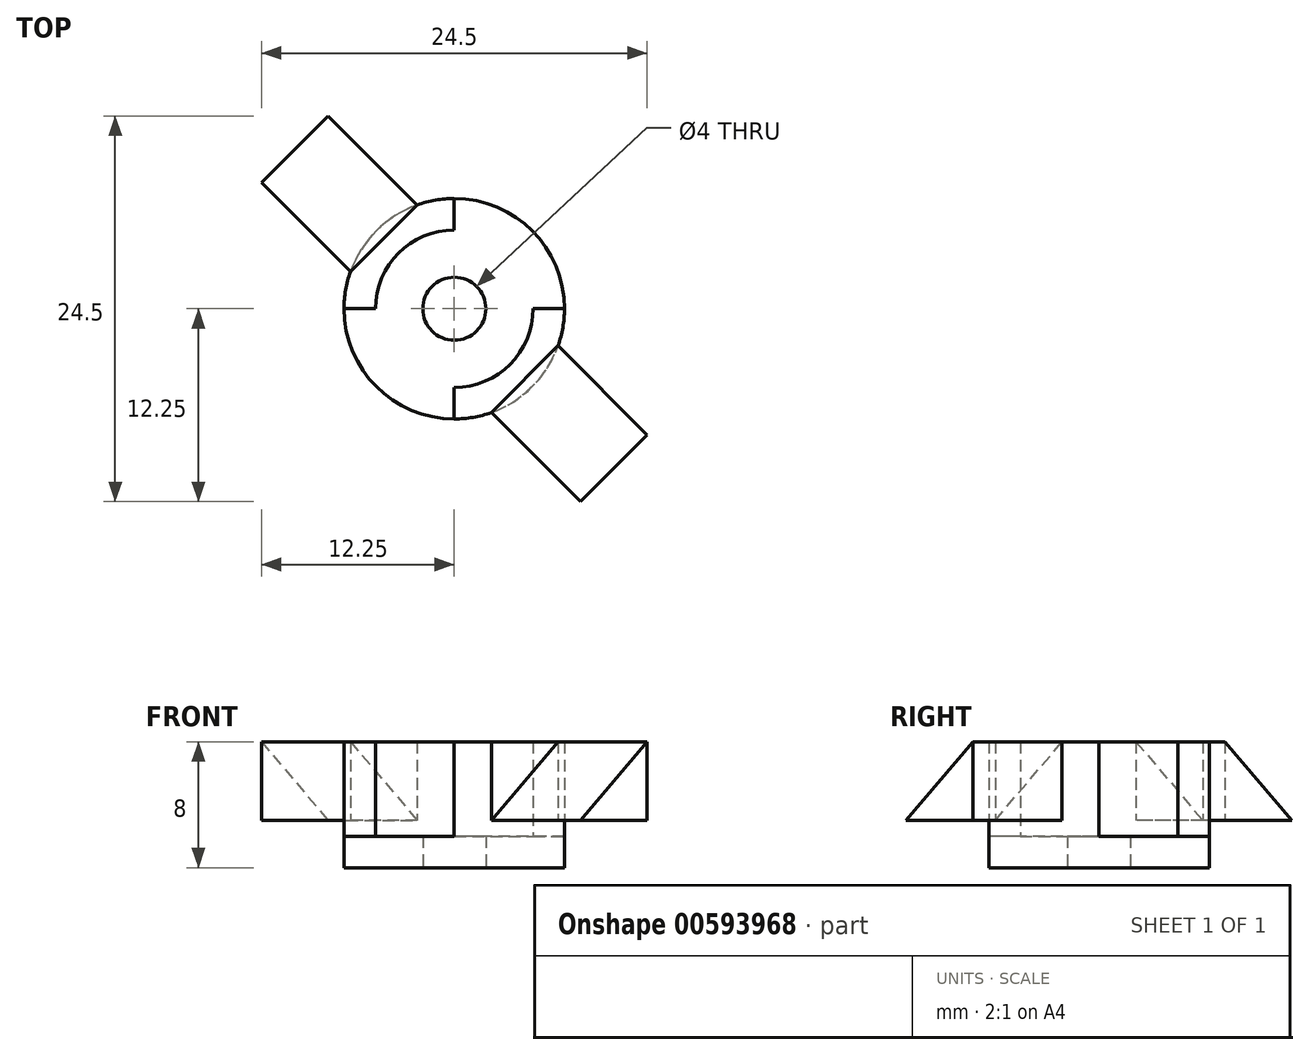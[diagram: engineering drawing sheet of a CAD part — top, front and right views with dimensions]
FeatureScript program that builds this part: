
annotation { "Feature Type Name" : "Feature", "Feature Type Description" : "" }
export const myFeature = defineFeature(function(context is Context, id is Id, definition is map)
    precondition{}
    {
        {
            var Q0;
            Q0=qCreatedBy(makeId("Top.planeOp"),FACE);
            var sketch = newSketch(context, id + "F0", { "sketchPlane" : qUnion([Q0])});
            skCircle(sketch, "E0", {"center": v(0, 0) * mm, "radius": 5 * mm});
            skCircle(sketch, "E1", {"center": v(0, 0) * mm, "radius": 7 * mm});
            skLineSegment(sketch, "E2", {"start": v(-5, 0) * mm, "end": v(-7, 0) * mm});
            skLineSegment(sketch, "E3.1.0", {"start": v(0, 5) * mm, "end": v(0, 7) * mm});
            skLineSegment(sketch, "E3.2.0", {"start": v(5, 0) * mm, "end": v(7, 0) * mm});
            skLineSegment(sketch, "E3.3.0", {"start": v(0, -5) * mm, "end": v(0, -7) * mm});
            skLineSegment(sketch, "E3.anchor1", {"start": v(0, 0) * mm, "end": v(-7, 0) * mm, "construction": true});
            skLineSegment(sketch, "E3.anchor2", {"start": v(0, 0) * mm, "end": v(0, -7) * mm, "construction": true});
            skCircle(sketch, "E4", {"center": v(0, 0) * mm, "radius": 2 * mm});
            skSolve(sketch);
        }
        {
            var Q0;
            {var subQ0=sQuery(id+"F0.wireOp",EDGE,"E2");Q0=makeQuery(id+"F0.imprint","IMPRINT",FACE,{"disambiguationData":[TD([[makeQuery(id+"F0.imprint","IMPRINT",EDGE,{"derivedFrom":subQ0}),-1.0]])]});}
            var Q1;
            {var subQ0=sQuery(id+"F0.wireOp",EDGE,"E3.1.0");Q1=makeQuery(id+"F0.imprint","IMPRINT",FACE,{"disambiguationData":[TD([[makeQuery(id+"F0.imprint","IMPRINT",EDGE,{"derivedFrom":subQ0}),-1.0]])]});}
            var Q2;
            {var subQ0=sQuery(id+"F0.wireOp",EDGE,"E3.2.0");Q2=makeQuery(id+"F0.imprint","IMPRINT",FACE,{"disambiguationData":[TD([[makeQuery(id+"F0.imprint","IMPRINT",EDGE,{"derivedFrom":subQ0}),-1.0]])]});}
            var Q3;
            {var subQ0=sQuery(id+"F0.wireOp",EDGE,"E2");Q3=makeQuery(id+"F0.imprint","IMPRINT",FACE,{"disambiguationData":[TD([[makeQuery(id+"F0.imprint","IMPRINT",EDGE,{"derivedFrom":subQ0}),1.0]])]});}
            var Q4;
            Q4=makeQuery(id+"F0.imprint","IMPRINT",FACE,{"disambiguationData":[TD([[makeQuery(id+"F0.imprint","IMPRINT",EDGE,{"derivedFrom":sQuery(id+"F0.wireOp",EDGE,"E4")}),-1.0]])]});
            extrude(context, id + "F1", {"entities" : qUnion([Q0, Q1, Q2, Q3, Q4]), "depth" : 2 * mm, "offsetDistance" : 25 * mm});
        }
        {
            var Q0;
            Q0=makeQuery(id+"F1.opExtrude","CAP_FACE",FACE,{"disambiguationData":[OSD([sQuery(id+"F0.wireOp",EDGE,"E1"),sQuery(id+"F0.wireOp",EDGE,"E4")])],"isStart":false});
            var sketch = newSketch(context, id + "F2", { "sketchPlane" : qUnion([Q0])});
            skCircle(sketch, "E5.0", {"center": v(0, 0) * mm, "radius": 5 * mm});
            skCircle(sketch, "E5.1", {"center": v(0, 0) * mm, "radius": 7 * mm});
            skLineSegment(sketch, "E5.2", {"start": v(-5, 0) * mm, "end": v(-7, 0) * mm});
            skLineSegment(sketch, "E5.3", {"start": v(0, 5) * mm, "end": v(0, 7) * mm});
            skLineSegment(sketch, "E5.4", {"start": v(5, 0) * mm, "end": v(7, 0) * mm});
            skLineSegment(sketch, "E5.5", {"start": v(0, -5) * mm, "end": v(0, -7) * mm});
            skPoint(sketch, "E5.6", {"position": v(0, 0) * mm});
            skLineSegment(sketch, "E5.7", {"start": v(0, 0) * mm, "end": v(-7, 0) * mm});
            skLineSegment(sketch, "E5.8", {"start": v(0, 0) * mm, "end": v(0, -7) * mm});
            skCircle(sketch, "E5.9", {"center": v(0, 0) * mm, "radius": 2 * mm});
            skLineSegment(sketch, "E6", {"start": v(-6.6, 2.35) * mm, "end": v(-2.35, 6.6) * mm});
            skLineSegment(sketch, "E7", {"start": v(2.35, -6.6) * mm, "end": v(6.6, -2.35) * mm});
            skSolve(sketch);
        }
        {
            var Q0;
            {var subQ0=sQuery(id+"F2.wireOp",EDGE,"E5.3");Q0=makeQuery(id+"F2.imprint","IMPRINT",FACE,{"disambiguationData":[TD([[makeQuery(id+"F2.imprint","IMPRINT",EDGE,{"derivedFrom":subQ0}),1.0]])]});}
            var Q1;
            {var subQ0=sQuery(id+"F2.wireOp",EDGE,"E6");Q1=makeQuery(id+"F2.imprint","IMPRINT",FACE,{"disambiguationData":[TD([[makeQuery(id+"F2.imprint","IMPRINT",EDGE,{"derivedFrom":subQ0}),1.0]])]});}
            var Q2;
            {var subQ0=sQuery(id+"F2.wireOp",EDGE,"E7");Q2=makeQuery(id+"F2.imprint","IMPRINT",FACE,{"disambiguationData":[TD([[makeQuery(id+"F2.imprint","IMPRINT",EDGE,{"derivedFrom":subQ0}),-1.0]])]});}
            var Q3;
            {var subQ0=sQuery(id+"F2.wireOp",EDGE,"E5.4");Q3=makeQuery(id+"F2.imprint","IMPRINT",FACE,{"disambiguationData":[TD([[makeQuery(id+"F2.imprint","IMPRINT",EDGE,{"derivedFrom":subQ0}),-1.0]])]});}
            extrude(context, id + "F3", {"entities" : qUnion([Q0, Q1, Q2, Q3]), "operationType" : NewBodyOperationType.ADD, "depth" : 1 * mm, "offsetDistance" : 25 * mm});
        }
        {
            var Q0;
            Q0=makeQuery(id+"F3.opExtrude","CAP_FACE",FACE,{"disambiguationData":[OSD([sQuery(id+"F2.wireOp",EDGE,"E5.0"),sQuery(id+"F2.wireOp",EDGE,"E5.1")])],"isStart":false});
            var sketch = newSketch(context, id + "F4", { "sketchPlane" : qUnion([Q0])});
            skCircle(sketch, "E8.0", {"center": v(0, 0) * mm, "radius": 5 * mm});
            skCircle(sketch, "E8.1", {"center": v(0, 0) * mm, "radius": 7 * mm});
            skLineSegment(sketch, "E8.2", {"start": v(-5, 0) * mm, "end": v(-7, 0) * mm});
            skLineSegment(sketch, "E8.3", {"start": v(0, 5) * mm, "end": v(0, 7) * mm});
            skLineSegment(sketch, "E8.4", {"start": v(5, 0) * mm, "end": v(7, 0) * mm});
            skLineSegment(sketch, "E8.5", {"start": v(0, -5) * mm, "end": v(0, -7) * mm});
            skPoint(sketch, "E8.6", {"position": v(0, 0) * mm});
            skLineSegment(sketch, "E8.7", {"start": v(0, 0) * mm, "end": v(-7, 0) * mm});
            skLineSegment(sketch, "E8.8", {"start": v(0, 0) * mm, "end": v(0, -7) * mm});
            skCircle(sketch, "E8.9", {"center": v(0, 0) * mm, "radius": 2 * mm});
            skLineSegment(sketch, "E8.10", {"start": v(-6.6, 2.35) * mm, "end": v(-2.35, 6.6) * mm});
            skLineSegment(sketch, "E8.11", {"start": v(2.35, -6.6) * mm, "end": v(6.6, -2.35) * mm});
            skSolve(sketch);
        }
        {
            var Q0;
            {var subQ0=sQuery(id+"F4.wireOp",EDGE,"E8.3");Q0=makeQuery(id+"F4.imprint","IMPRINT",FACE,{"disambiguationData":[TD([[makeQuery(id+"F4.imprint","IMPRINT",EDGE,{"derivedFrom":subQ0}),1.0]])]});}
            var Q1;
            {var subQ0=sQuery(id+"F4.wireOp",EDGE,"E8.4");Q1=makeQuery(id+"F4.imprint","IMPRINT",FACE,{"disambiguationData":[TD([[makeQuery(id+"F4.imprint","IMPRINT",EDGE,{"derivedFrom":subQ0}),-1.0]])]});}
            extrude(context, id + "F5", {"entities" : qUnion([Q0, Q1]), "operationType" : NewBodyOperationType.ADD, "depth" : 5 * mm, "offsetDistance" : 25 * mm});
        }
        {
            var Q0;
            Q0=makeQuery(id+"F5.opExtrude","SWEPT_FACE",FACE,{"disambiguationData":[OSD([sQuery(id+"F4.wireOp",EDGE,"E8.10")])]});
            var sketch = newSketch(context, id + "F6", { "sketchPlane" : qUnion([Q0])});
            skPoint(sketch, "E9", {"position": v(3, 8) * mm});
            skPoint(sketch, "E10", {"position": v(3, 3) * mm});
            skPoint(sketch, "E11", {"position": v(-3, 3) * mm});
            skPoint(sketch, "E12", {"position": v(-3, 8) * mm});
            skLineSegment(sketch, "E13", {"start": v(-3, 8) * mm, "end": v(3, 3) * mm});
            skLineSegment(sketch, "E14", {"start": v(3, 8) * mm, "end": v(-3, 3) * mm});
            skPoint(sketch, "E15", {"position": v(0, 5.5) * mm});
            skCircle(sketch, "E16", {"center": v(0, 5.5) * mm, "radius": 1.5 * mm});
            skSolve(sketch);
        }
        {
            var Q0;
            Q0=makeQuery(id+"F5.opExtrude","SWEPT_FACE",FACE,{"disambiguationData":[OSD([sQuery(id+"F4.wireOp",EDGE,"E8.11")])]});
            var sketch = newSketch(context, id + "F7", { "sketchPlane" : qUnion([Q0])});
            skPoint(sketch, "E17", {"position": v(-3, 3) * mm});
            skPoint(sketch, "E18", {"position": v(-3, 8) * mm});
            skPoint(sketch, "E19", {"position": v(3, 8) * mm});
            skPoint(sketch, "E20", {"position": v(3, 3) * mm});
            skLineSegment(sketch, "E21", {"start": v(-3, 8) * mm, "end": v(3, 3) * mm});
            skLineSegment(sketch, "E22", {"start": v(-3, 3) * mm, "end": v(3, 8) * mm});
            skCircle(sketch, "E23", {"center": v(0, 5.5) * mm, "radius": 1.5 * mm});
            skSolve(sketch);
        }
        {
            var Q0;
            {var subQ0=sQuery(id+"F7.wireOp",EDGE,"E22");var subQ1=sQuery(id+"F7.wireOp",EDGE,"E21");var subQ2=makeQuery(id+"F7.imprint","INTERSECT",VERTEX,{"derivedFrom":[subQ1,subQ0]});Q0=makeQuery(id+"F7.imprint","IMPRINT",FACE,{"disambiguationData":[TD([[makeQuery(id+"F7.imprint","IMPRINT",EDGE,{"disambiguationData":[TD([[subQ2,-1.0]])],"derivedFrom":subQ1}),1.0]])]});}
            var Q1;
            {var subQ0=sQuery(id+"F7.wireOp",EDGE,"E23");var subQ1=sQuery(id+"F7.wireOp",EDGE,"E21");var subQ2=makeQuery(id+"F7.imprint","INTERSECT",VERTEX,{"disambiguationData":[OD(0.0)],"derivedFrom":[subQ1,subQ0]});Q1=makeQuery(id+"F7.imprint","IMPRINT",FACE,{"disambiguationData":[TD([[makeQuery(id+"F7.imprint","IMPRINT",EDGE,{"disambiguationData":[TD([[subQ2,-1.0]])],"derivedFrom":subQ1}),-1.0]])]});}
            var Q2;
            {var subQ0=sQuery(id+"F7.wireOp",EDGE,"E23");var subQ1=sQuery(id+"F7.wireOp",EDGE,"E21");var subQ2=makeQuery(id+"F7.imprint","INTERSECT",VERTEX,{"disambiguationData":[OD(0.0)],"derivedFrom":[subQ1,subQ0]});Q2=makeQuery(id+"F7.imprint","IMPRINT",FACE,{"disambiguationData":[TD([[makeQuery(id+"F7.imprint","IMPRINT",EDGE,{"disambiguationData":[TD([[subQ2,-1.0]])],"derivedFrom":subQ1}),1.0]])]});}
            var Q3;
            {var subQ0=sQuery(id+"F7.wireOp",EDGE,"E22");var subQ1=sQuery(id+"F7.wireOp",EDGE,"E21");var subQ2=makeQuery(id+"F7.imprint","INTERSECT",VERTEX,{"derivedFrom":[subQ1,subQ0]});Q3=makeQuery(id+"F7.imprint","IMPRINT",FACE,{"disambiguationData":[TD([[makeQuery(id+"F7.imprint","IMPRINT",EDGE,{"disambiguationData":[TD([[subQ2,-1.0]])],"derivedFrom":subQ1}),-1.0]])]});}
            extrude(context, id + "F8", {"entities" : qUnion([Q0, Q1, Q2, Q3]), "operationType" : NewBodyOperationType.ADD, "depth" : 8 * mm, "offsetDistance" : 25 * mm});
        }
        {
            var Q0;
            {var subQ0=sQuery(id+"F6.wireOp",EDGE,"E16");var subQ1=sQuery(id+"F6.wireOp",EDGE,"E13");var subQ2=makeQuery(id+"F6.imprint","INTERSECT",VERTEX,{"disambiguationData":[OD(0.0)],"derivedFrom":[subQ1,subQ0]});Q0=makeQuery(id+"F6.imprint","IMPRINT",FACE,{"disambiguationData":[TD([[makeQuery(id+"F6.imprint","IMPRINT",EDGE,{"disambiguationData":[TD([[subQ2,-1.0]])],"derivedFrom":subQ1}),1.0]])]});}
            var Q1;
            {var subQ0=sQuery(id+"F6.wireOp",EDGE,"E14");var subQ1=sQuery(id+"F6.wireOp",EDGE,"E13");var subQ2=makeQuery(id+"F6.imprint","INTERSECT",VERTEX,{"derivedFrom":[subQ1,subQ0]});Q1=makeQuery(id+"F6.imprint","IMPRINT",FACE,{"disambiguationData":[TD([[makeQuery(id+"F6.imprint","IMPRINT",EDGE,{"disambiguationData":[TD([[subQ2,-1.0]])],"derivedFrom":subQ1}),1.0]])]});}
            var Q2;
            {var subQ0=sQuery(id+"F6.wireOp",EDGE,"E14");var subQ1=sQuery(id+"F6.wireOp",EDGE,"E13");var subQ2=makeQuery(id+"F6.imprint","INTERSECT",VERTEX,{"derivedFrom":[subQ1,subQ0]});Q2=makeQuery(id+"F6.imprint","IMPRINT",FACE,{"disambiguationData":[TD([[makeQuery(id+"F6.imprint","IMPRINT",EDGE,{"disambiguationData":[TD([[subQ2,-1.0]])],"derivedFrom":subQ1}),-1.0]])]});}
            var Q3;
            {var subQ0=sQuery(id+"F6.wireOp",EDGE,"E16");var subQ1=sQuery(id+"F6.wireOp",EDGE,"E13");var subQ2=makeQuery(id+"F6.imprint","INTERSECT",VERTEX,{"disambiguationData":[OD(0.0)],"derivedFrom":[subQ1,subQ0]});Q3=makeQuery(id+"F6.imprint","IMPRINT",FACE,{"disambiguationData":[TD([[makeQuery(id+"F6.imprint","IMPRINT",EDGE,{"disambiguationData":[TD([[subQ2,-1.0]])],"derivedFrom":subQ1}),-1.0]])]});}
            extrude(context, id + "F9", {"entities" : qUnion([Q0, Q1, Q2, Q3]), "operationType" : NewBodyOperationType.ADD, "depth" : 8 * mm, "offsetDistance" : 25 * mm});
        }
    });
